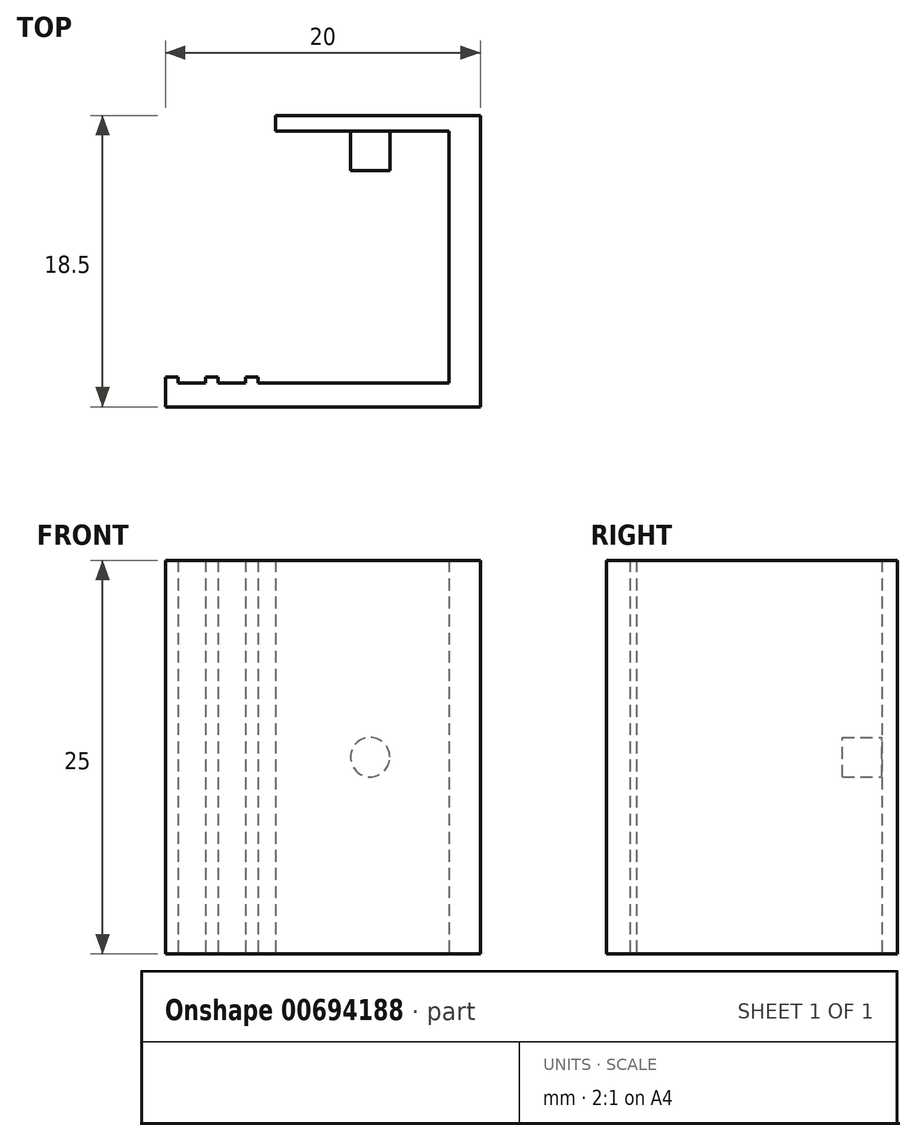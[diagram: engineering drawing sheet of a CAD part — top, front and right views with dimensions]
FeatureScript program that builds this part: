
annotation { "Feature Type Name" : "Feature", "Feature Type Description" : "" }
export const myFeature = defineFeature(function(context is Context, id is Id, definition is map)
    precondition{}
    {
        {
            var Q0;
            Q0=qCreatedBy(makeId("Top.planeOp"),FACE);
            var sketch = newSketch(context, id + "F0", { "sketchPlane" : qUnion([Q0])});
            skLineSegment(sketch, "E0", {"start": v(23.16, 6.58) * mm, "end": v(36.16, 6.58) * mm});
            skLineSegment(sketch, "E1", {"start": v(36.16, 6.58) * mm, "end": v(36.16, -11.92) * mm});
            skLineSegment(sketch, "E2", {"start": v(36.16, -11.92) * mm, "end": v(16.16, -11.92) * mm});
            skLineSegment(sketch, "E3", {"start": v(16.16, -11.92) * mm, "end": v(16.16, -10.42) * mm});
            skLineSegment(sketch, "E4", {"start": v(16.96, -10.42) * mm, "end": v(18.7, -10.42) * mm});
            skLineSegment(sketch, "E5", {"start": v(34.16, -10.42) * mm, "end": v(34.16, 5.58) * mm});
            skLineSegment(sketch, "E6", {"start": v(23.16, 5.58) * mm, "end": v(23.16, 6.58) * mm});
            skLineSegment(sketch, "E7.trimOffspring", {"start": v(28.36, 5.58) * mm, "end": v(23.16, 5.58) * mm});
            skLineSegment(sketch, "E8", {"start": v(30.16, 5.58) * mm, "end": v(34.16, 5.58) * mm});
            skLineSegment(sketch, "E9.top", {"start": v(16.16, -10.02) * mm, "end": v(16.96, -10.02) * mm});
            skLineSegment(sketch, "E9.left", {"start": v(16.16, -10.42) * mm, "end": v(16.16, -10.02) * mm});
            skLineSegment(sketch, "E9.right", {"start": v(16.96, -10.42) * mm, "end": v(16.96, -10.02) * mm});
            skLineSegment(sketch, "E10.top", {"start": v(18.7, -10.02) * mm, "end": v(19.5, -10.02) * mm});
            skLineSegment(sketch, "E10.left", {"start": v(18.7, -10.42) * mm, "end": v(18.7, -10.02) * mm});
            skLineSegment(sketch, "E10.right", {"start": v(19.5, -10.42) * mm, "end": v(19.5, -10.02) * mm});
            skLineSegment(sketch, "E11.top", {"start": v(21.24, -10.02) * mm, "end": v(22.04, -10.02) * mm});
            skLineSegment(sketch, "E11.left", {"start": v(22.04, -10.42) * mm, "end": v(22.04, -10.02) * mm});
            skLineSegment(sketch, "E11.right", {"start": v(21.24, -10.42) * mm, "end": v(21.24, -10.02) * mm});
            skLineSegment(sketch, "E12.trimOffspring", {"start": v(19.5, -10.42) * mm, "end": v(21.24, -10.42) * mm});
            skLineSegment(sketch, "E13.trimOffspring", {"start": v(22.04, -10.42) * mm, "end": v(34.16, -10.42) * mm});
            skLineSegment(sketch, "E14", {"start": v(30.16, 5.58) * mm, "end": v(28.36, 5.58) * mm});
            skSolve(sketch);
        }
        {
            var Q0;
            Q0=makeQuery(id+"F0.imprint","IMPRINT",FACE,{"disambiguationData":[TD([[makeQuery(id+"F0.imprint","IMPRINT",EDGE,{"derivedFrom":sQuery(id+"F0.wireOp",EDGE,"E0")}),-1.0]])]});
            extrude(context, id + "F1", {"entities" : qUnion([Q0]), "depth" : 25 * mm, "offsetDistance" : 25 * mm});
        }
        {
            var Q0;
            Q0=makeQuery(id+"F1.opExtrude","SWEPT_FACE",FACE,{"disambiguationData":[OSD([sQuery(id+"F0.wireOp",EDGE,"E7.trimOffspring"),sQuery(id+"F0.wireOp",EDGE,"E8"),sQuery(id+"F0.wireOp",EDGE,"E14")])]});
            var sketch = newSketch(context, id + "F2", { "sketchPlane" : qUnion([Q0])});
            skCircle(sketch, "E15", {"center": v(29.16, 12.5) * mm, "radius": 1.25 * mm});
            skSolve(sketch);
        }
        {
            var Q0;
            Q0=makeQuery(id+"F2.imprint","IMPRINT",FACE,{"disambiguationData":[TD([[makeQuery(id+"F2.imprint","IMPRINT",EDGE,{"derivedFrom":sQuery(id+"F2.wireOp",EDGE,"E15")}),1.0]])]});
            extrude(context, id + "F3", {"entities" : qUnion([Q0]), "operationType" : NewBodyOperationType.ADD, "depth" : 2.5 * mm, "offsetDistance" : 25 * mm});
        }
    });
